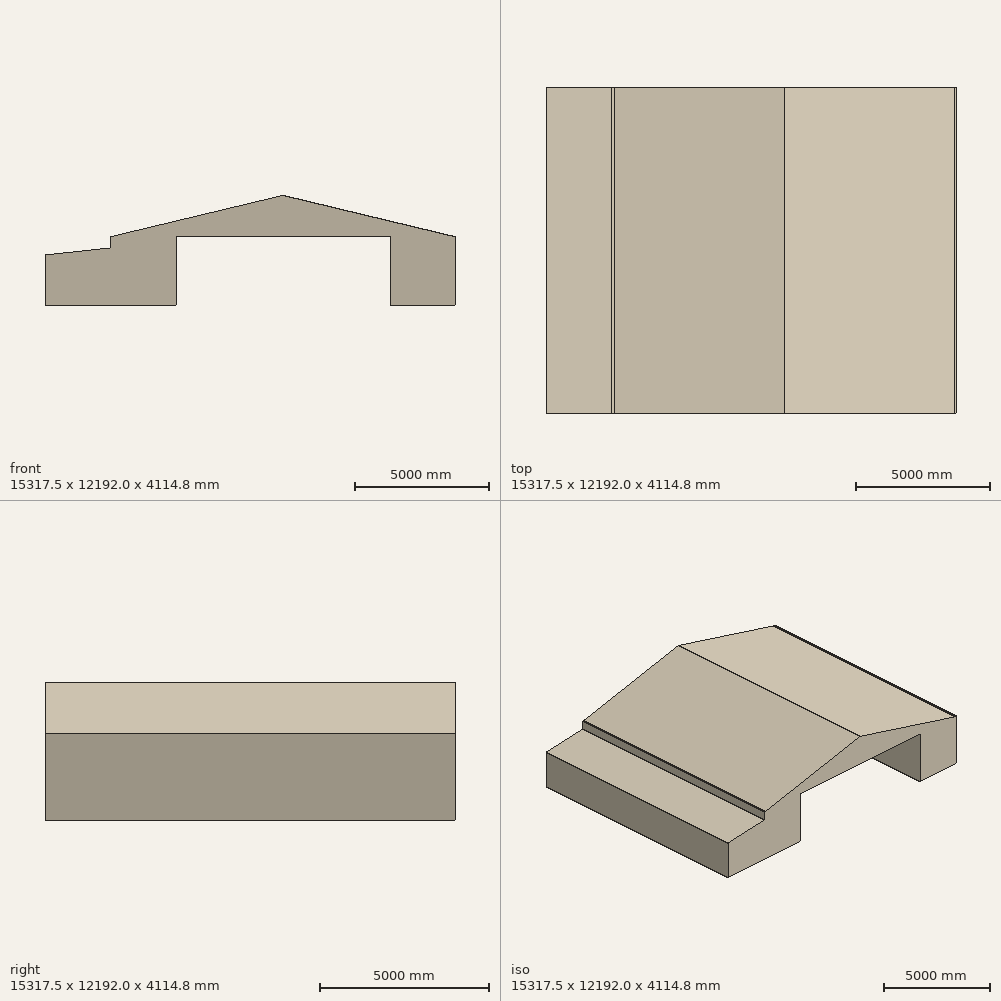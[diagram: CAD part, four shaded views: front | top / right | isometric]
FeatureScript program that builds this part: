
annotation { "Feature Type Name" : "Feature", "Feature Type Description" : "" }
export const myFeature = defineFeature(function(context is Context, id is Id, definition is map)
    precondition{}
    {
        {
            var Q0;
            Q0=qCreatedBy(makeId("Front.planeOp"),FACE);
            var sketch = newSketch(context, id + "F0", { "sketchPlane" : qUnion([Q0])});
            skLineSegment(sketch, "E0.bottom", {"start": v(-4001.13, 1295.4) * mm, "end": v(-6439.53, 1295.4) * mm});
            skLineSegment(sketch, "E0.top", {"start": v(-4001.13, -1295.4) * mm, "end": v(-6439.53, -1295.4) * mm});
            skLineSegment(sketch, "E0.left", {"start": v(-4001.13, 1295.4) * mm, "end": v(-4001.13, -1295.4) * mm});
            skLineSegment(sketch, "E0.right", {"start": v(-6439.53, 1295.4) * mm, "end": v(-6439.53, -1295.4) * mm});
            skPoint(sketch, "E0.middle", {"position": v(-5220.33, 0) * mm});
            skPoint(sketch, "E1.middle", {"position": v(-62.2, 0) * mm});
            skPoint(sketch, "E1.top.end.orphan", {"position": v(-2338.73, -2276.53) * mm});
            skPoint(sketch, "E1.top.start.orphan", {"position": v(2214.34, -2276.53) * mm});
            skPoint(sketch, "E1.bottom.end.orphan", {"position": v(-2338.73, 2276.53) * mm});
            skPoint(sketch, "E1.bottom.start.orphan", {"position": v(2214.34, 2276.53) * mm});
            skLineSegment(sketch, "E2", {"start": v(-4001.13, 1295.4) * mm, "end": v(5142.87, 1295.4) * mm});
            skLineSegment(sketch, "E3", {"start": v(0, 1295.4) * mm, "end": v(0, 1792.59) * mm});
            skLineSegment(sketch, "E4.MirrorCS", {"start": v(4001.13, 1295.4) * mm, "end": v(4001.13, -1295.4) * mm});
            skLineSegment(sketch, "E5.MirrorCS", {"start": v(4001.13, 1295.4) * mm, "end": v(6439.53, 1295.4) * mm});
            skLineSegment(sketch, "E6.MirrorCS", {"start": v(6439.53, 1295.4) * mm, "end": v(6439.53, -1295.4) * mm});
            skLineSegment(sketch, "E7.MirrorCS", {"start": v(4001.13, -1295.4) * mm, "end": v(6439.53, -1295.4) * mm});
            skLineSegment(sketch, "E8", {"start": v(0, 1295.4) * mm, "end": v(0, 2819.4) * mm});
            skLineSegment(sketch, "E9", {"start": v(0, 2819.4) * mm, "end": v(-6858, 1172.94) * mm});
            skLineSegment(sketch, "E10.MirrorCS", {"start": v(0, 2819.4) * mm, "end": v(6858, 1172.94) * mm});
            skLineSegment(sketch, "E11", {"start": v(-6439.53, 857.96) * mm, "end": v(-8877.93, 594.36) * mm});
            skLineSegment(sketch, "E12", {"start": v(-6439.53, -1295.4) * mm, "end": v(-10320.84, -1295.4) * mm});
            skLineSegment(sketch, "E13", {"start": v(-8877.93, 594.36) * mm, "end": v(-8877.93, -1295.4) * mm});
            skSolve(sketch);
        }
        {
            var Q0;
            Q0 = qSketchRegion(id + "F0", true);
            extrude(context, id + "F1", {"entities" : qUnion([Q0]), "depth" : 12192 * mm});
        }
        {
            var Q0;
            Q0 = qSketchRegion(id + "F0", true);
            extrude(context, id + "F2", {"entities" : qUnion([Q0]), "operationType" : NewBodyOperationType.ADD, "depth" : 12192 * mm, "offsetDistance" : 30.48 * mm});
        }
    });
